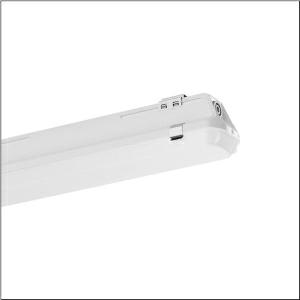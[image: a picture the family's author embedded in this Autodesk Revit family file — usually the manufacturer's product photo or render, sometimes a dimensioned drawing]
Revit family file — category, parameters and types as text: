
# Revit family: monsun_r__11_51fp12mp480h_cfdd
name_source: partatom
category: Lighting Fixtures
units: mm (PartAtom-declared; Revit-internal decimal feet)

## family parameters
Cut with Voids When Loaded = No
Host = Face
Light Source = No
Part Type = Normal
Room Calculation Point = No
Round Connector Dimension = Use Diameter
Shared = No

## types (1)
- --- (1 x LED, 7990 lm, 45.4 W, 4000K)
    Apparent Load = 45 VA
    CIE Flux Codes = 65 88 97 97 100
    Color Rendering = 80
    Color Temperature = 4000K
    Default Elevation = 1800 mm
    Description = Monsun® 11, damp-proof luminaire, chain hanger, primary light control with lens, primary optical cover: enclosure, of PMMA, light emission: direct distribution, primary light characteristic: symmetric, installation type: suspended mounting, surface-mounted, horizontal mounting, vertical mounting, LED, rated luminous flux: 7.990lm, luminous efficacy: 176lm/W, light colour: 840, colour temperature: 4000K, control gear: ECG, with terminal, 3-pole, max. 2.5mm², mains connection: 220..240V, AC, 50/60Hz, rated input power: 45W, luminaire housing, of glass-fibre reinforced polyester, uncoated, bright grey, incl. chain hanger, length: 1.590mm, width: 90mm, height: 88mm, clip for enclosure, of stainless steel (V2A), ceiling mounting element, of stainless steel (V2A), chain hanger, of stainless steel (V2A), protection rating (complete): IP66, insulation class (complete): insulation class I (protective earthing), certification: CE, ENEC, VDE, UKCA, protection symbol: D, impact resistance: IK04, permissible operating ambient temperature: -35..+40°C, standard: EN 50419, EN 60598-2-1, no direct snow, no direct sun, no direct rain, for indoor or canopied outdoor use, corresponds to IFS (International Featured Standards) requirements for safety and quality in the food industry, contact your sales advisor before using the luminaires in applications with unclear chemical exposure, large temperature fluctuations or condensation-forming humidity, LABS conformity tested according to VDMA 24364:2018-05, packaging unit: 1 piece
    Height = 89 mm
    Lamp = 1 x LED
    Lamp Light Flux = 7990 lm
    Lamp Power = 45.4 W
    Lamp count = 1
    Length = 1590 mm
    Luminous efficacy = 176 lm/W
    Manufacturer = Siteco
    ModVariant = No
    Model = 51FP12MP480H
    Mounting Place = Ceiling
    Mounting Type = Surface mounted
    Number of Poles = 1
    OnlyDefault = Yes
    Power Factor = 1
    Product Name = Monsun® 11
    Product group = damp-proof luminaire
    ProductGroupID = 300
    Protection Class = Protection class I
    Protection Degree = IP 66
    RLX_Detail_Level = 1
    RLX_Emergency_Light_Flux = 0 lm
    RLX_Emergency_Type = 0
    RLX_Emergency_Type_DB = No
    RlxData = <blob elided: 89705 chars, md5=512dd320>
    Socket = socket
    Standby Power = 0 W
    System Light Flux = 7990 lm
    System Power = 45 W
    Type Comments = factory setting: luminous flux: 100 % | (A | C | E) | 105 mA
    Type Image = l_1319650.jpg
    URL = http://relux.com
    VarID = @adj_174657
    Voltage = 0 V
    Weight = 0.00 kg
    Width = 90 mm

## geometry (parser evidence)
native form markers: Blend x4, Sweep x10
no freeform markers — native parametric forms only
